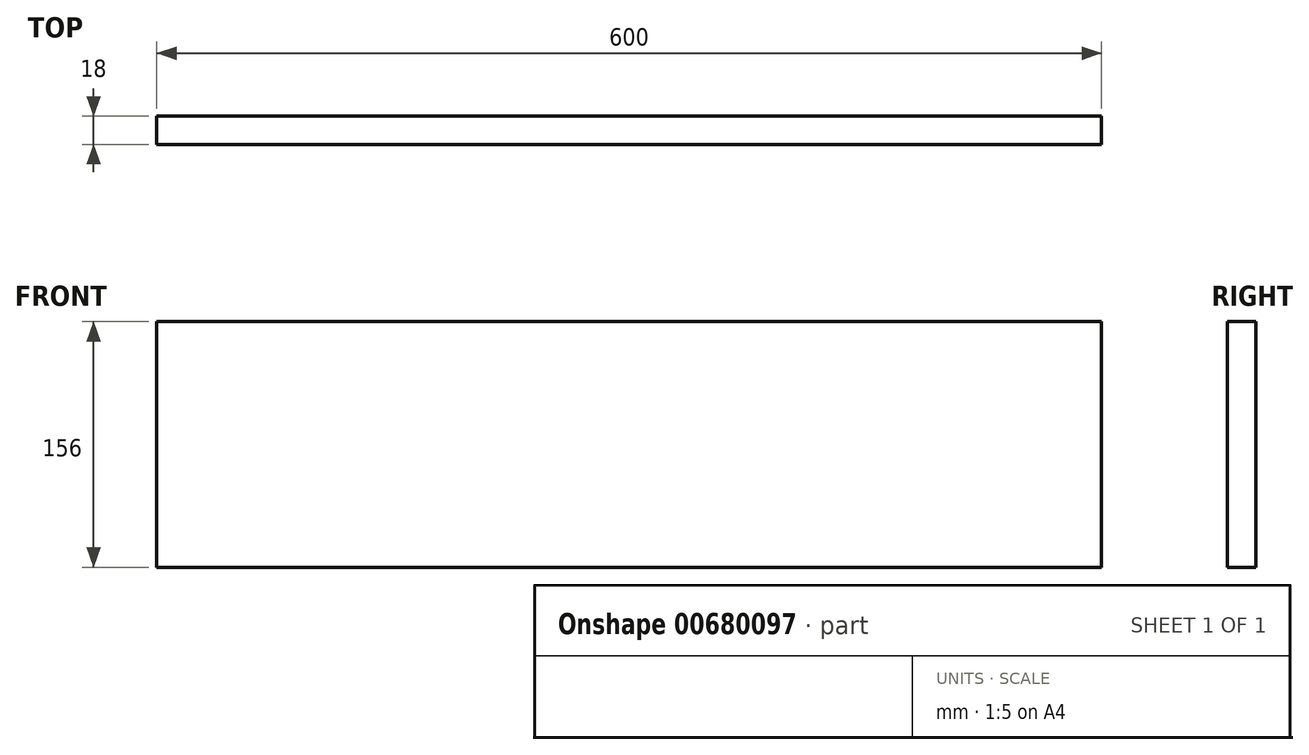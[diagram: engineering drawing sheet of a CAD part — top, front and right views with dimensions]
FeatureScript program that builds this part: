
annotation { "Feature Type Name" : "Feature", "Feature Type Description" : "" }
export const myFeature = defineFeature(function(context is Context, id is Id, definition is map)
    precondition{}
    {
        {
            var Q0;
            Q0=qCreatedBy(makeId("Front.planeOp"),FACE);
            var sketch = newSketch(context, id + "F0", { "sketchPlane" : qUnion([Q0])});
            skLineSegment(sketch, "E0.bottom", {"start": v(-300, -78) * mm, "end": v(300, -78) * mm});
            skLineSegment(sketch, "E0.top", {"start": v(-300, 78) * mm, "end": v(300, 78) * mm});
            skLineSegment(sketch, "E0.left", {"start": v(-300, -78) * mm, "end": v(-300, 78) * mm});
            skLineSegment(sketch, "E0.right", {"start": v(300, -78) * mm, "end": v(300, 78) * mm});
            skPoint(sketch, "E0.middle", {"position": v(0, 0) * mm});
            skSolve(sketch);
        }
        {
            var Q0;
            Q0=makeQuery(id+"F0.imprint","IMPRINT",FACE,{"disambiguationData":[TD([[makeQuery(id+"F0.imprint","IMPRINT",EDGE,{"derivedFrom":sQuery(id+"F0.wireOp",EDGE,"E0.bottom")}),1.0]])]});
            extrude(context, id + "F1", {"entities" : qUnion([Q0]), "endBound" : BoundingType.SYMMETRIC, "depth" : 18 * mm, "offsetDistance" : 25 * mm});
        }
    });
